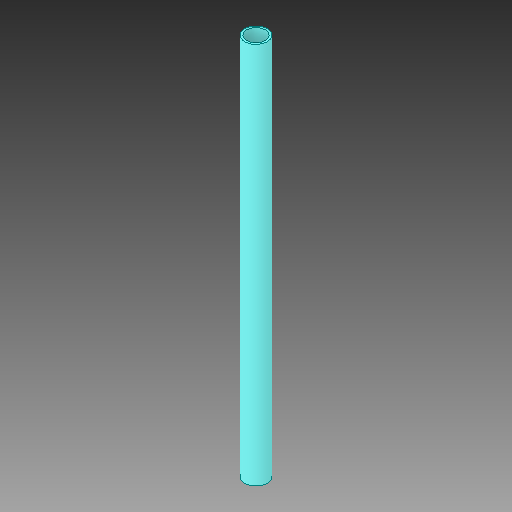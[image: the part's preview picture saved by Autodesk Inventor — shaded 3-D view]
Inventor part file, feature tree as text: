
AUTODESK INVENTOR PART (.ipt)
format: ipt  version: 2018 (Build 220112000, 112)  size: 75,776 bytes
history: native  units: in
note: dims shown in document units (in); Inventor stores cm internally (conversion verified against a paired STEP export)
features: extrude x1, sketch x1
ambient origin geometry x8: Origin, YZ Plane, XZ Plane, XY Plane, X Axis, Y Axis, Z Axis, Center Point
bodies: Solid1 (feature_tree)
feature tree (2):
  extrude  "Extrusion1"  Depth=6.329in
  sketch  "Sketch1"  dims[d0=0.375in d1=0.31in d2=6.329in d3=0.0in]
